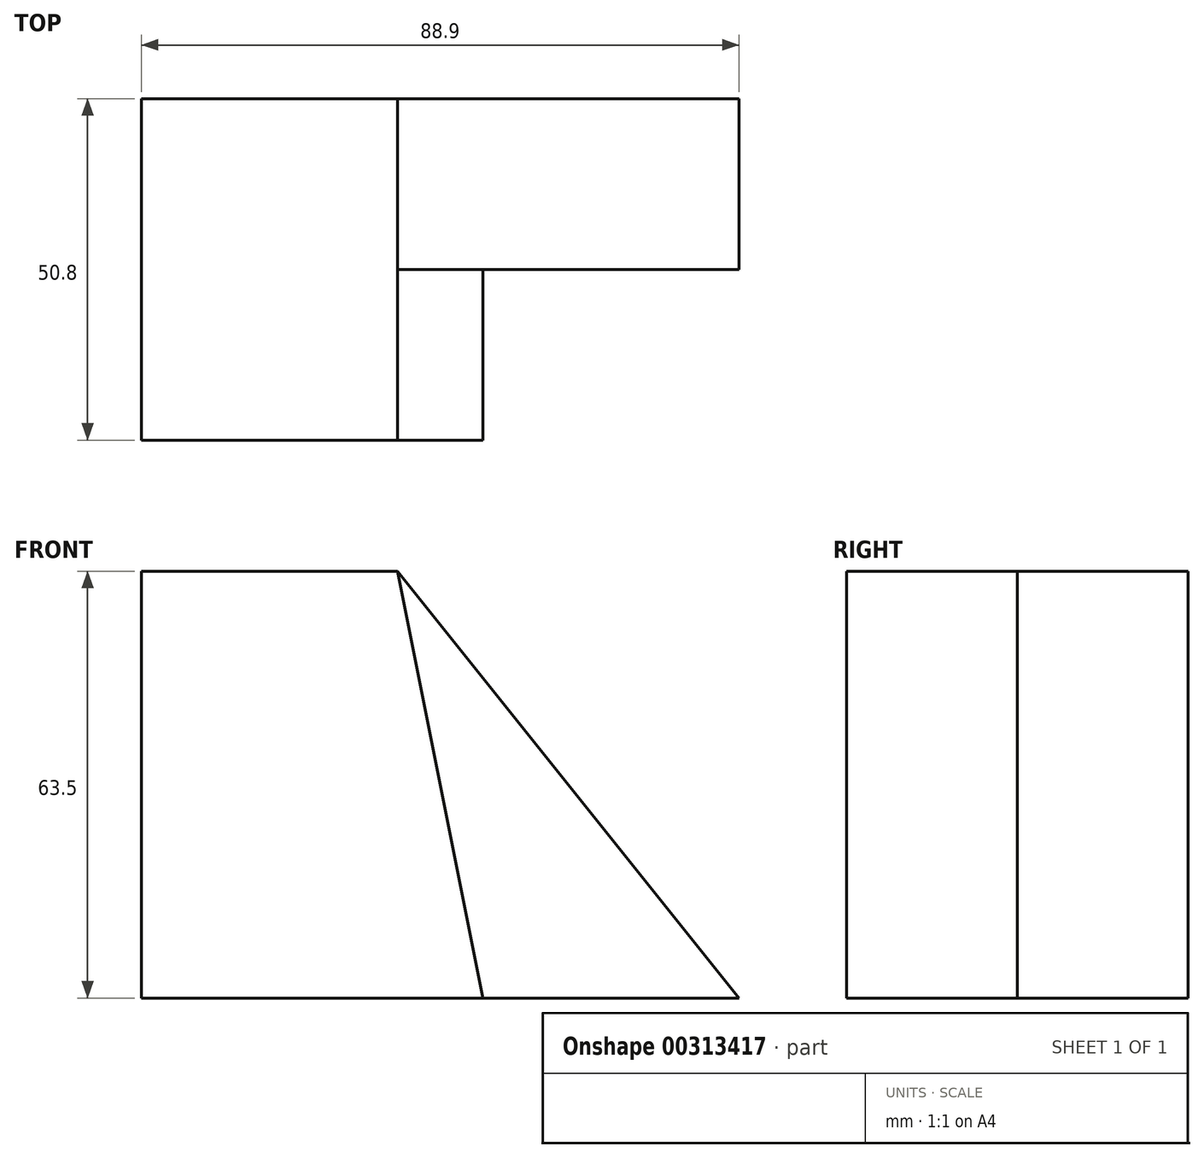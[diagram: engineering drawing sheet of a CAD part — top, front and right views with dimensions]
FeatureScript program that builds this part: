
annotation { "Feature Type Name" : "Feature", "Feature Type Description" : "" }
export const myFeature = defineFeature(function(context is Context, id is Id, definition is map)
    precondition{}
    {
        {
            var Q0;
            Q0=qCreatedBy(makeId("Front.planeOp"),FACE);
            var sketch = newSketch(context, id + "F0", { "sketchPlane" : qUnion([Q0])});
            skLineSegment(sketch, "E0", {"start": v(-22.7, -46.35) * mm, "end": v(28.1, -46.35) * mm});
            skLineSegment(sketch, "E1", {"start": v(-22.7, -46.35) * mm, "end": v(-22.7, 17.15) * mm});
            skLineSegment(sketch, "E2", {"start": v(-22.7, 17.15) * mm, "end": v(15.4, 17.15) * mm});
            skLineSegment(sketch, "E3", {"start": v(15.4, 17.15) * mm, "end": v(28.1, -46.35) * mm});
            skSolve(sketch);
        }
        {
            var Q0;
            Q0=makeQuery(id+"F0.imprint","IMPRINT",FACE,{"disambiguationData":[TD([[makeQuery(id+"F0.imprint","IMPRINT",EDGE,{"derivedFrom":sQuery(id+"F0.wireOp",EDGE,"E0")}),1.0]])]});
            extrude(context, id + "F1", {"entities" : qUnion([Q0]), "depth" : 25.4 * mm});
        }
        {
            var Q0;
            Q0=makeQuery(id+"F1.opExtrude","CAP_FACE",FACE,{"disambiguationData":[OSD([sQuery(id+"F0.wireOp",EDGE,"E0"),sQuery(id+"F0.wireOp",EDGE,"E1"),sQuery(id+"F0.wireOp",EDGE,"E2"),sQuery(id+"F0.wireOp",EDGE,"E3")])],"isStart":true});
            var sketch = newSketch(context, id + "F2", { "sketchPlane" : qUnion([Q0])});
            skLineSegment(sketch, "E4", {"start": v(22.7, -46.35) * mm, "end": v(-66.2, -46.35) * mm});
            skLineSegment(sketch, "E5", {"start": v(22.7, 17.15) * mm, "end": v(-15.4, 17.15) * mm});
            skLineSegment(sketch, "E6", {"start": v(-15.4, 17.15) * mm, "end": v(-66.2, -46.35) * mm});
            skSolve(sketch);
        }
        {
            var Q0;
            {var subQ2=sQuery(id+"F2.wireOp",EDGE,"E6");Q0=makeQuery(id+"F2.imprint","IMPRINT",FACE,{"disambiguationData":[TD([[makeQuery(id+"F2.imprint","IMPRINT",EDGE,{"derivedFrom":subQ2}),1.0]])]});}
            var Q1;
            Q1=makeQuery(id+"F2.imprint","IMPRINT",FACE,{"disambiguationData":[TD([[makeQuery(id+"F2.imprint","IMPRINT",EDGE,{"derivedFrom":sQuery(id+"F2.wireOp",EDGE,"E5")}),1.0]])]});
            extrude(context, id + "F3", {"entities" : qUnion([Q0, Q1]), "operationType" : NewBodyOperationType.ADD, "depth" : 25.4 * mm});
        }
    });
